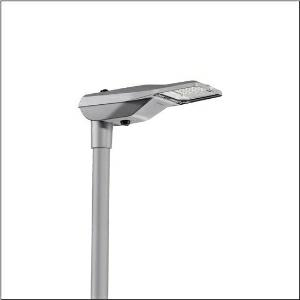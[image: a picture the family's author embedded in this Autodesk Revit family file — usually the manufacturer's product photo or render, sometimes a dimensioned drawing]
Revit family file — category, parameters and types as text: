
# Revit family: streetlight_sl_21_iq_micro___st1_0a_5xe1d61y08db_6c32
name_source: partatom
category: Lighting Fixtures
units: mm (PartAtom-declared; Revit-internal decimal feet)

## family parameters
Cut with Voids When Loaded = No
Host = Face
Light Source = No
Part Type = Normal
Room Calculation Point = No
Round Connector Dimension = Use Diameter
Shared = No

## types (1)
- --- (1 x LED, 4430 lm, 39.1 W, 2700K)
    Apparent Load = 39 VA
    CIE Flux Codes = 37 72 97 100 100
    Color Rendering = 70
    Color Temperature = 2700K
    Default Elevation = 1800 mm
    Description = Streetlight SL 21 iQ micro, mast luminaire, primary light control with lens, of PMMA, primary optical cover: cover, of toughened safety glass, transparent, light distribution: ST1.0a, light emission: direct distribution, primary light characteristic: asymmetric, installation type: post-top, side-entry, LED, High Power LED, rated luminous flux: 4.430lm, luminous efficacy: 113lm/W, light colour: 727, colour temperature: 2700K, control gear: iQ-Street Remote, D4i with power reduction, control: pre-setting: logarithmic dimming characteristic, Street-Remote, Auto-Match, Temp-Guard, Lumen-Switch, Night-Set, Smart-Wire, Light-Fading, Desk-Remote (wireless, voltage-free reading and setting of iQ features in the workshop via application-optimized NFC function/RFID function), optimised constant luminous flux control (CLO 2.0), mains connection: 220..240V, AC, 50/60Hz, start of lifetime: 39W, end of service life: 41W, reduction: 17W, luminaire housing, of diecast aluminium, powder-coated, Siteco® metallic grey (DB 702S), corrosivity category C5 mid according to DIN EN ISO 12944, please order mast flange separately, inclination adjustable: 0°, 5°, 10°, 15°, sealing non-destructively replaceable, multi-level sealing system, length: 528mm, width: 235mm, height: 110mm, mast flange for spigot size: 42mm (side-entry): 5XC10008XM4, 60/48mm (side-entry/post-top): 5XC10108XM2, 76/60mm (side-entry/post-top): 5XC10108XM1, mounting height: 4..8m, Smart Interface below and above, protection rating (complete): IP66, insulation class (complete): insulation class II (safety insulation), certification: CE, ENEC, ENEC+, VDE, impact resistance: IK10, permissible operating ambient temperature for outdoor applications: -40..+50°C, standard-compliant lighting for roads and squares, packaging unit: 1 piece

Light Distribution: ST1.0a
    Height = 110 mm
    Lamp = 1 x LED
    Lamp Light Flux = 4430 lm
    Lamp Power = 39.1 W
    Lamp count = 1
    Length = 528 mm
    Luminous efficacy = 113 lm/W
    Manufacturer = Siteco
    ModVariant = No
    Model = 5XE1D61Y08DB
    Number of Poles = 1
    OnlyDefault = Yes
    Power Factor = 1
    Product Name = Streetlight SL 21 iQ micro | ST1.0a
    Product group = mast luminaire | pylon top
    ProductGroupID = 6100
    Protection Class = Protection class II
    Protection Degree = IP 66
    RLX_Detail_Level = 1
    RLX_Emergency_Light_Flux = 0 lm
    RLX_Emergency_Type = 0
    RLX_Emergency_Type_DB = No
    RlxData = <blob elided: 98729 chars, md5=97de0640>
    Socket = socket
    Standby Power = 0 W
    System Light Flux = 4430 lm
    System Power = 39 W
    Type Comments = factory setting: luminous flux: 100 % | dim-lin: 254 | 765 mA
    Type Image = l_1007239.jpg
    URL = http://relux.com
    VarID = @adj_115494
    Voltage = 0 V
    Weight = 0.00 kg
    Width = 235 mm

## geometry (parser evidence)
native form markers: Blend x4, Sweep x11
no freeform markers — native parametric forms only
